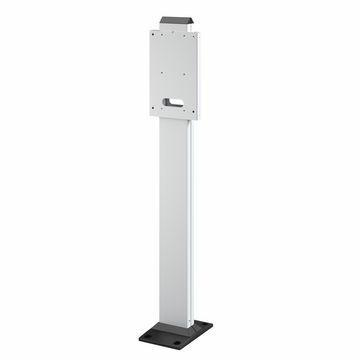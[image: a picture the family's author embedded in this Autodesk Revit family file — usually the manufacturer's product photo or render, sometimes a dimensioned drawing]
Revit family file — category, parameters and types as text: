
# Revit family: Building-RicaricaVeicoliElettrici-GEWISS-JOINON-ICON_SUPPORTO-PAVIM-MONOFACC
name_source: partatom
category: Apparecchi elettrici
units: mm (PartAtom-declared; Revit-internal decimal feet)

## family parameters
Condiviso = No
Host = Superficie
Mantenere orientamento annotazione = Sì
Punto di calcolo locali = Sì
Quota connettore circolare = Usa diametro
Taglio con vuoti quando caricato = No
Tipo di parte = Normale

## types (1)
- GWJ8102 - SUPPORTO PAVIMENTO I-CON - MONOFACCIALE
    Adatto per = WallBox I-CON
    BLOCCO = B=C
    Catalogo = E-MOBILITY
    Codice EAN = 8034035071379
    Codice Electrocod = 2242
    Descrizione = SUPPORTO PAVIMENTO I-CON - MONOFACCIALE
    Descrizione: = Supporto pavimento I-CON - monofacciale
    FORMULA = 1000 mm  [stored 3.28084 ft]
    IDF = 8bd9f2f6-5ab0-40bc-a2ae-4c982108b16b
    IDT = 9d8fff42-0005-4008-88f3-94fb88b800ce
    Immagine tipo = ICON_SUPP_MONO.jpg
    L = 155 mm  [stored 0.50853 ft]
    Modello = GWJ8102
    N.poli = 1
    POMELLO = bianco
    PRESA = Giallo
    Produttore = GEWISS S.p.A.
    Prospetto di default = 1219 mm
    STRUTTURA = RAL - 7035
    STRUTTURA ALTA = blue
    Scheda Tecnica = https://www.gewiss.com
    Spostamento_S = 1500 mm  [stored 4.92126 ft]
    URL = https://www.gewiss.com
    VETRO = Vetro
    Versione file RFA = 19.4
    Voltaggio = 0 V
    W = 115 mm  [stored 0.377297 ft]

note: [stored X ft] marks values corroborated as IEEE doubles in the binary element streams (Revit-internal decimal feet)
